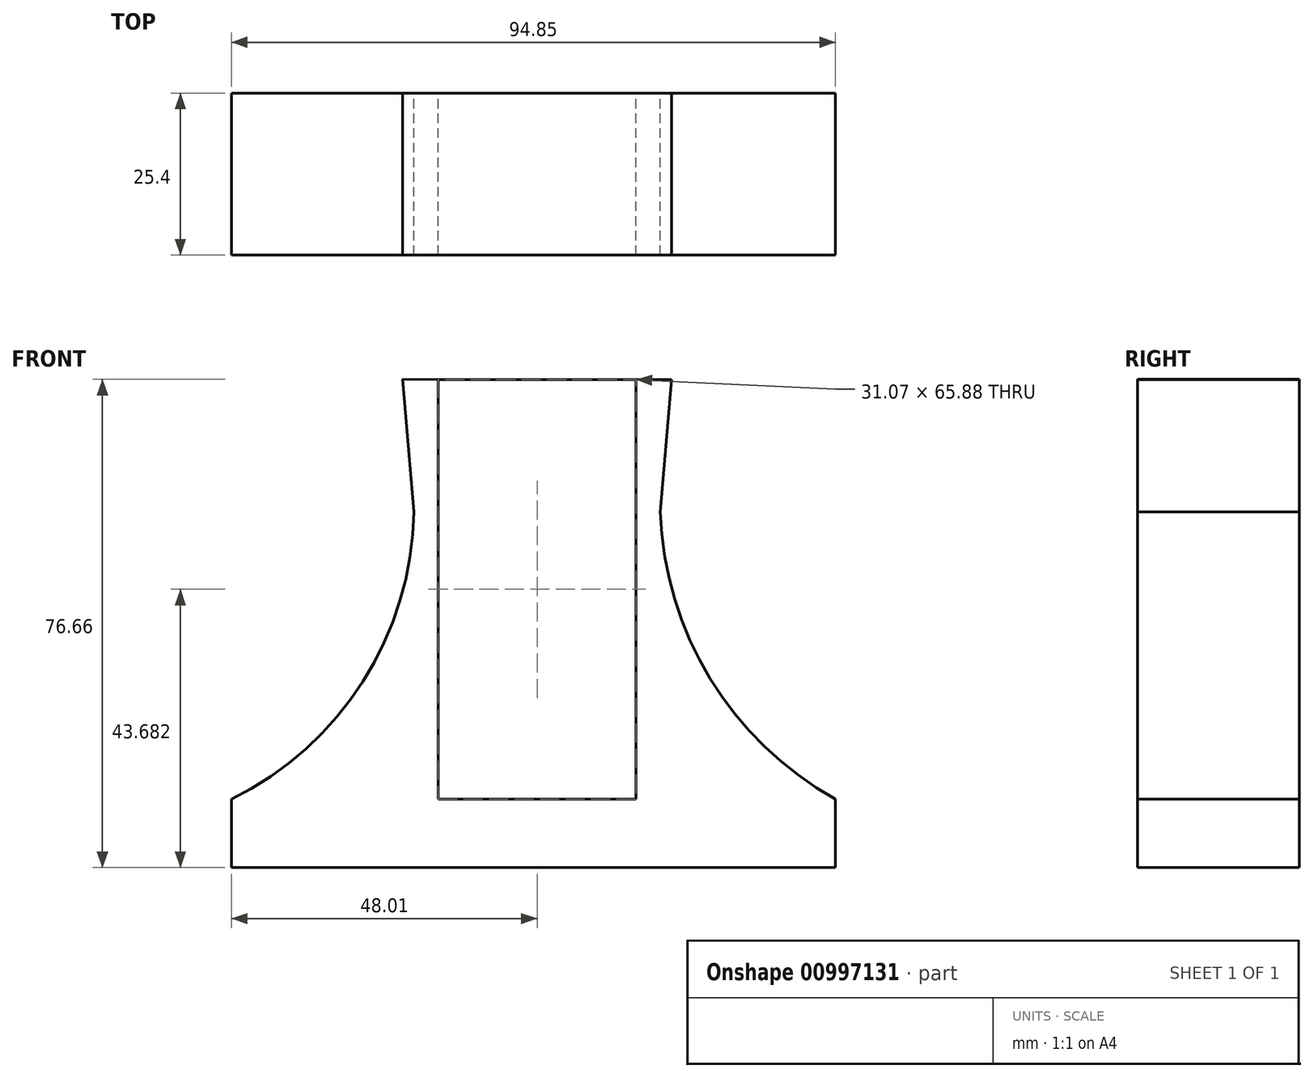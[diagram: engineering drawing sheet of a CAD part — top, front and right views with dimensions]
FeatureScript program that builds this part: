
annotation { "Feature Type Name" : "Feature", "Feature Type Description" : "" }
export const myFeature = defineFeature(function(context is Context, id is Id, definition is map)
    precondition{}
    {
        {
            var Q0;
            Q0=qCreatedBy(makeId("Front.planeOp"),FACE);
            var sketch = newSketch(context, id + "F0", { "sketchPlane" : qUnion([Q0])});
            skLineSegment(sketch, "E0", {"start": v(0, -45.09) * mm, "end": v(0, -45.09) * mm});
            skLineSegment(sketch, "E1.bottom", {"start": v(0, -45.09) * mm, "end": v(-15.53, -45.09) * mm});
            skLineSegment(sketch, "E1.top", {"start": v(0, 20.8) * mm, "end": v(-15.53, 20.8) * mm});
            skLineSegment(sketch, "E1.left", {"start": v(0, -45.09) * mm, "end": v(0, 20.8) * mm});
            skLineSegment(sketch, "E1.right", {"start": v(-15.53, -45.09) * mm, "end": v(-15.53, 20.8) * mm});
            skLineSegment(sketch, "E2.bottom", {"start": v(0, -45.09) * mm, "end": v(15.53, -45.09) * mm});
            skLineSegment(sketch, "E2.top", {"start": v(0, 20.8) * mm, "end": v(15.53, 20.8) * mm});
            skLineSegment(sketch, "E2.right", {"start": v(15.53, -45.09) * mm, "end": v(15.53, 20.8) * mm});
            skLineSegment(sketch, "E3", {"start": v(-21.1, 20.83) * mm, "end": v(-15.53, -45.09) * mm});
            skLineSegment(sketch, "E4", {"start": v(21.1, 21.07) * mm, "end": v(15.53, -45.09) * mm});
            skLineSegment(sketch, "E5.bottom", {"start": v(0, -45.09) * mm, "end": v(-48, -45.09) * mm});
            skLineSegment(sketch, "E5.top", {"start": v(0, -55.83) * mm, "end": v(-48, -55.83) * mm});
            skLineSegment(sketch, "E5.left", {"start": v(0, -45.09) * mm, "end": v(0, -55.83) * mm});
            skLineSegment(sketch, "E5.right", {"start": v(-48, -45.09) * mm, "end": v(-48, -55.83) * mm});
            skLineSegment(sketch, "E6.bottom", {"start": v(-48, -55.83) * mm, "end": v(46.84, -55.83) * mm});
            skLineSegment(sketch, "E6.top", {"start": v(-48, -45.09) * mm, "end": v(46.84, -45.09) * mm});
            skLineSegment(sketch, "E6.left", {"start": v(-48, -55.83) * mm, "end": v(-48, -45.09) * mm});
            skLineSegment(sketch, "E6.right", {"start": v(46.84, -55.83) * mm, "end": v(46.84, -45.09) * mm});
            skArc(sketch, "E7", {"start": v(-48, -45.09) * mm, "mid": v(-27.34, -26.57) * mm, "end": v(-19.35, 0) * mm});
            skArc(sketch, "E8", {"start": v(19.33, 0) * mm, "mid": v(27.16, -26.16) * mm, "end": v(46.84, -45.09) * mm});
            skLineSegment(sketch, "E9", {"start": v(-21.1, 20.83) * mm, "end": v(21.1, 20.8) * mm});
            skSolve(sketch);
        }
        {
            var Q0;
            Q0 = qSketchRegion(id + "F0", true);
            extrude(context, id + "F1", {"entities" : qUnion([Q0]), "depth" : 25.4 * mm, "offsetDistance" : 25.4 * mm});
        }
    });
